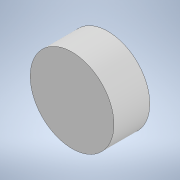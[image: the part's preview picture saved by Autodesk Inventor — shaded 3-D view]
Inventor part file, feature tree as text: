
AUTODESK INVENTOR PART (.ipt)
format: ipt  version: 2021 (Build 250183000, 183)  size: 91,648 bytes
history: native  units: mm
features: other x1, extrude x1, sketch x1
ambient origin geometry x8: Origin, YZ Plane, XZ Plane, XY Plane, X Axis, Y Axis, Z Axis, Center Point
bodies: Body1 (feature_tree)
feature tree (3):
  other  "Sólido1"
  extrude  "Extrusión1"  Depth=30.0mm TaperAngle=0.0deg
  sketch  "Boceto1"  dims[d0=70.0mm d1=30.0mm d2=0.0mm]
